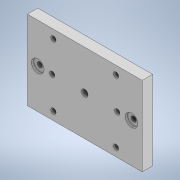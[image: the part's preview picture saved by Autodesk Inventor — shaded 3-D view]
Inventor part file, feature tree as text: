
AUTODESK INVENTOR PART (.ipt)
format: ipt  version: 2022.2 (Build 262287030, 287C)  size: 131,072 bytes
history: native  units: in
note: dims shown in document units (in); Inventor stores cm internally (conversion verified against a paired STEP export)
features: sketch x4, hole x3, extrude x1, projected_geometry x1
ambient origin geometry x8: Origin, YZ Plane, XZ Plane, XY Plane, X Axis, Y Axis, Z Axis, Center Point
bodies: Solid1 (feature_tree)
feature tree (9):
  extrude  "Extrusion1"  Depth=1.4961in
  hole  "Hole1"  [1 undecoded]
  hole  "Hole2"  [1 undecoded]
  hole  "Hole3"  [1 undecoded]
  sketch  "Sketch1"  dims[d0=0.1969in d1=0.0in d2=1.4961in]
  sketch  "Sketch2"  dims[d3=2.1654in d4=0.5906in]
  projected_geometry  "Projected Loop1"
  sketch  "Sketch3"  dims[d5=0.5906in d34=0.7874in d36=1.1811in d37=0.3937in d39=0.3937in]
  sketch  "Sketch4"  dims[d41=0.7874in d43=1.1811in d44=0.3937in d46=0.3937in d48=0.7874in d50=0.6142in d51=0.3937in d53=0.3937in d55=0.7874in d57=0.6142in d58=0.3937in d60=0.3937in d62=0.0984in d63=0.2953in d64=0.1476in d65=0.0984in d66=90.0deg d67=0.3937in d68=0.8108in d69=0.125in d70=0.2953in d71=0.1476in d72=0.0984in d73=90.0deg d74=0.3937in d75=0.8108in d76=0.1969in d77=0.1969in d78=0.0968in d79=0.2362in d80=0.2362in d81=0.0394in d82=90.0deg d83=0.3937in d84=0.8108in]
note: 3 required parameter values undecoded (feature->parameter linkage not recoverable at this tier; creation-order binding heuristic only, values carry confidence <= 0.55)
